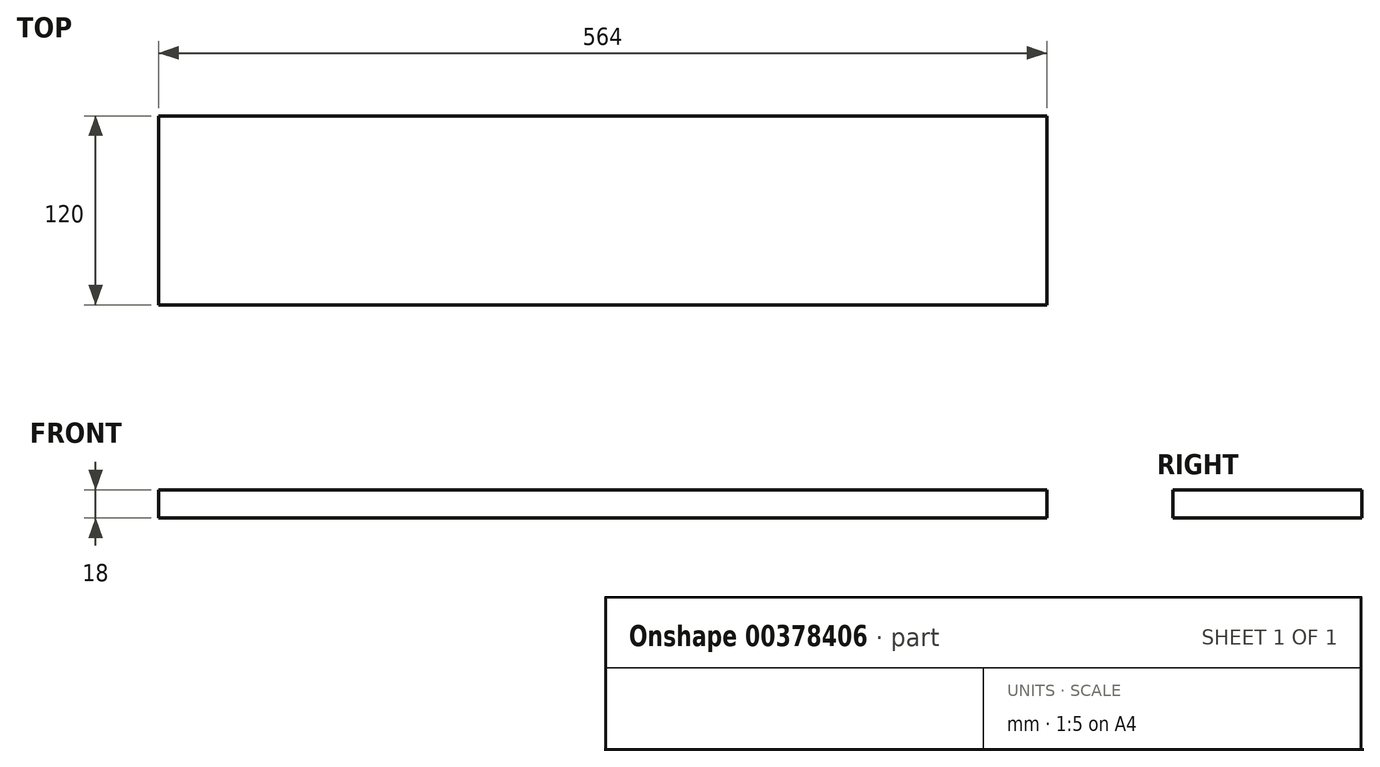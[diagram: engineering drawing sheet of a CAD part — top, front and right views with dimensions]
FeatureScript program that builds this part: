
annotation { "Feature Type Name" : "Feature", "Feature Type Description" : "" }
export const myFeature = defineFeature(function(context is Context, id is Id, definition is map)
    precondition{}
    {
        {
            var Q0;
            Q0=qCreatedBy(makeId("Right.planeOp"),FACE);
            var sketch = newSketch(context, id + "F0", { "sketchPlane" : qUnion([Q0])});
            skLineSegment(sketch, "E0.bottom", {"start": v(60, 9) * mm, "end": v(-60, 9) * mm});
            skLineSegment(sketch, "E0.top", {"start": v(60, -9) * mm, "end": v(-60, -9) * mm});
            skLineSegment(sketch, "E0.left", {"start": v(60, 9) * mm, "end": v(60, -9) * mm});
            skLineSegment(sketch, "E0.right", {"start": v(-60, 9) * mm, "end": v(-60, -9) * mm});
            skPoint(sketch, "E0.middle", {"position": v(0, 0) * mm});
            skSolve(sketch);
        }
        {
            var Q0;
            Q0=qSketchRegion(id+"F0",true);
            extrude(context, id + "F1", {"entities" : qUnion([Q0]), "depth" : 564 * mm});
        }
    });
